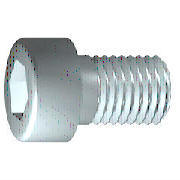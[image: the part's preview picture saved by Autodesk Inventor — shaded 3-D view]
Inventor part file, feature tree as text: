
AUTODESK INVENTOR PART (.ipt)
format: ipt  version: 2015 (Build 190159000, 159)  size: 193,024 bytes
history: native  units: mm (DEFAULTED — no unit token found)
features: sketch x2, extrude x1, plane x1, fillet x1
ambient origin geometry x7: Origin, YZ Plane, XY Plane, X Axis, Y Axis, Z Axis, Center Point
bodies: Solid1 (feature_tree), Body (feature_tree)
feature tree (5):
  extrude  "Slot"  Depth=8.0mm
  plane  "Work Plane1"
  fillet  "Fillet2"  Radius=8.0mm
  sketch  "Sketch1"  dims[d1=16.875mm d2=0.766912mm d3=8.0mm]
  sketch  "Sketch2"  dims[d4=4.0mm d5=60.0deg d6=8.0mm d7=8.0mm d8=6.928203mm d9=13.0mm d10=90.0deg d11=10.0mm d12=0.0mm d13=16.875mm d14=0.0mm d15=0.766813mm d16=0.766813mm d17=0.8mm d19=0.0mm d26=20.0mm d27=45.0deg d28=0.0mm d29=0.0mm d30=0.1mm]
